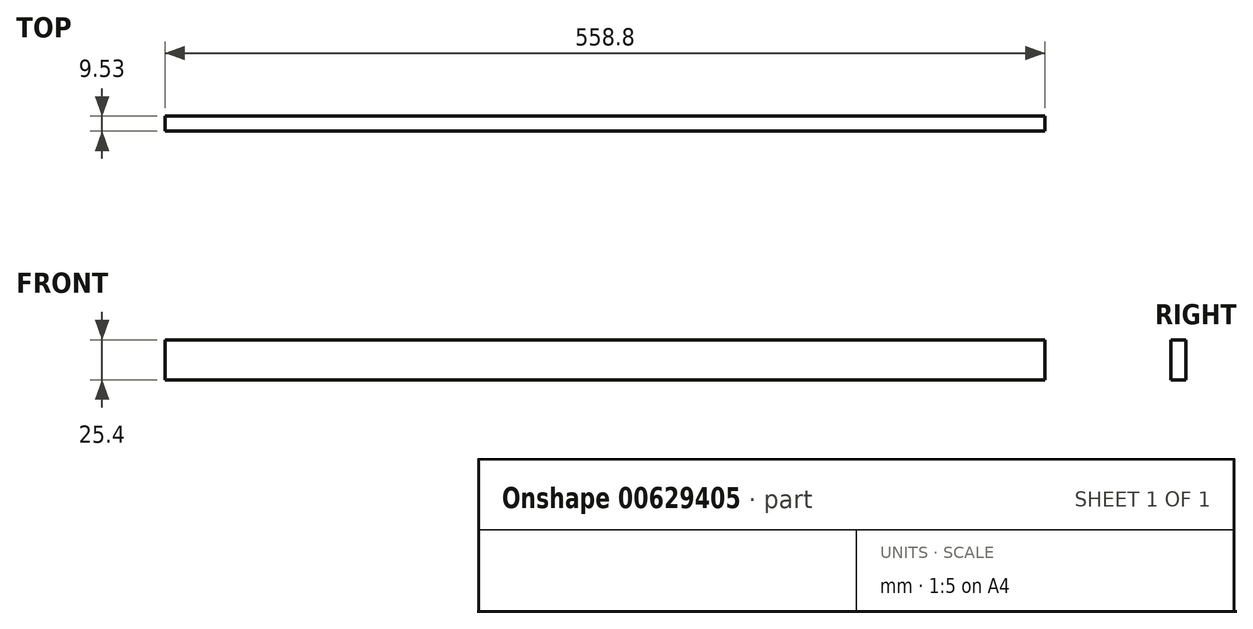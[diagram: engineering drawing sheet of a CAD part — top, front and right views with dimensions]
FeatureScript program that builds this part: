
annotation { "Feature Type Name" : "Feature", "Feature Type Description" : "" }
export const myFeature = defineFeature(function(context is Context, id is Id, definition is map)
    precondition{}
    {
        {
            var Q0;
            Q0=qCreatedBy(makeId("Front.planeOp"),FACE);
            var sketch = newSketch(context, id + "F0", { "sketchPlane" : qUnion([Q0])});
            skLineSegment(sketch, "E0.bottom", {"start": v(0, 0) * mm, "end": v(558.8, 0) * mm});
            skLineSegment(sketch, "E0.top", {"start": v(0, 25.4) * mm, "end": v(558.8, 25.4) * mm});
            skLineSegment(sketch, "E0.left", {"start": v(0, 0) * mm, "end": v(0, 25.4) * mm});
            skLineSegment(sketch, "E0.right", {"start": v(558.8, 0) * mm, "end": v(558.8, 25.4) * mm});
            skSolve(sketch);
        }
        {
            var Q0;
            Q0=qSketchRegion(id+"F0",true);
            extrude(context, id + "F1", {"entities" : qUnion([Q0]), "depth" : 9.52 * mm, "offsetDistance" : 25.4 * mm});
        }
    });
